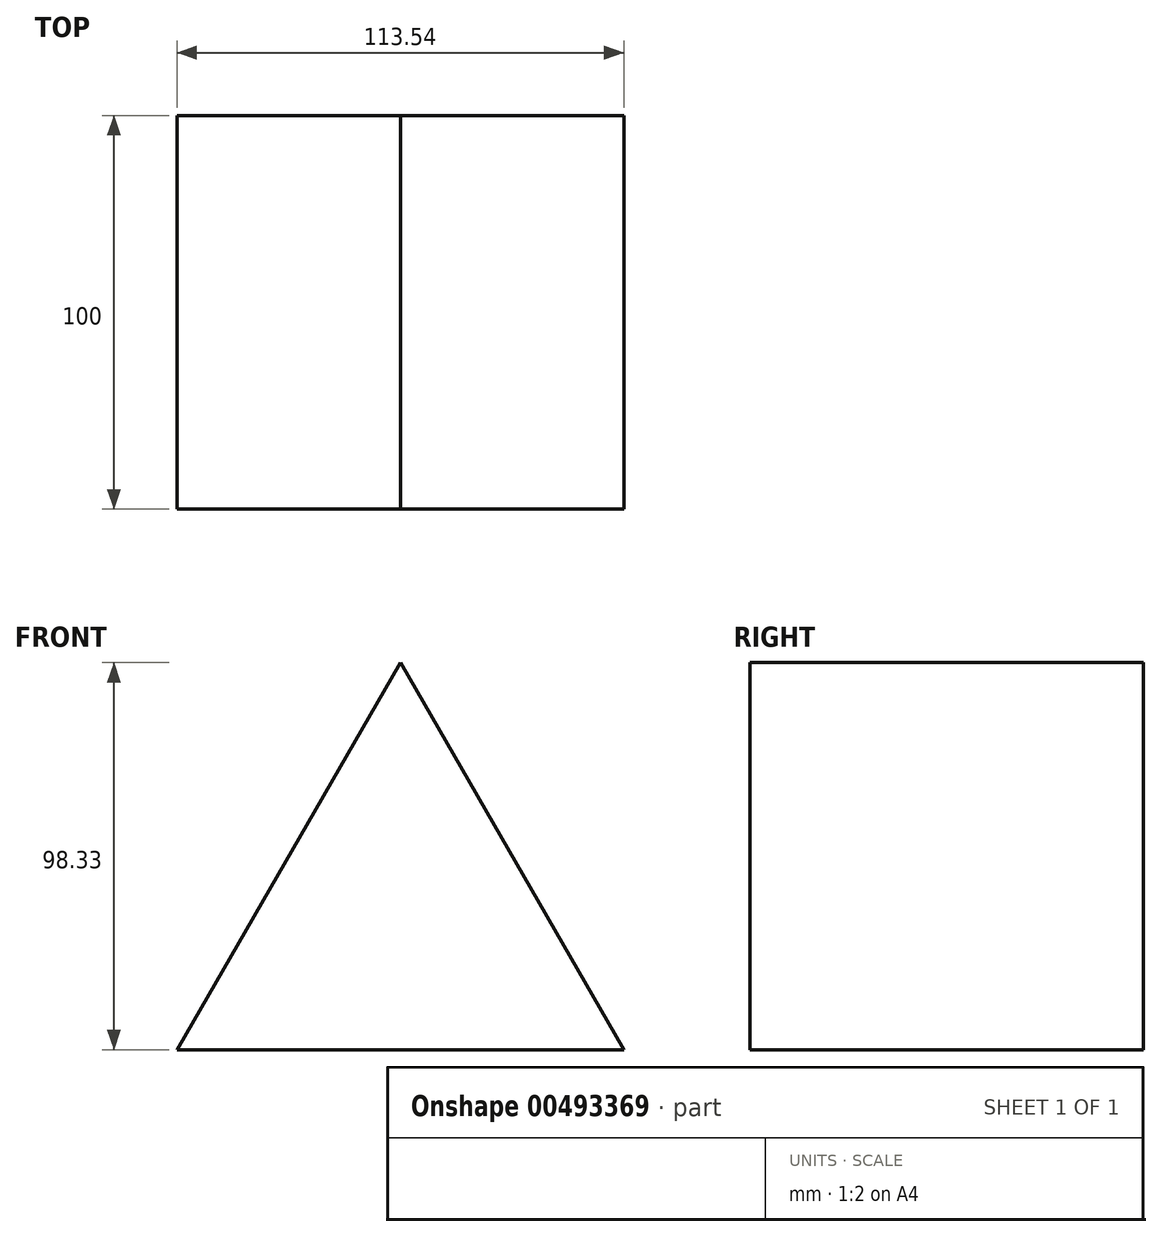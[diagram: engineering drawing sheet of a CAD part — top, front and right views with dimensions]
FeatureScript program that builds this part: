
annotation { "Feature Type Name" : "Feature", "Feature Type Description" : "" }
export const myFeature = defineFeature(function(context is Context, id is Id, definition is map)
    precondition{}
    {
        {
            var Q0;
            Q0=qCreatedBy(makeId("Front.planeOp"),FACE);
            var sketch = newSketch(context, id + "F0", { "sketchPlane" : qUnion([Q0])});
            skCircle(sketch, "E0.cCircle", {"center": v(0, 0) * mm, "radius": 65.55 * mm, "construction": true});
            skLineSegment(sketch, "E0.0", {"start": v(0, 65.55) * mm, "end": v(56.77, -32.78) * mm});
            skLineSegment(sketch, "E0.1", {"start": v(56.77, -32.78) * mm, "end": v(-56.77, -32.78) * mm});
            skLineSegment(sketch, "E0.2", {"start": v(-56.77, -32.78) * mm, "end": v(0, 65.55) * mm});
            skSolve(sketch);
        }
        {
            var Q0;
            Q0 = qSketchRegion(id + "F0", true);
            extrude(context, id + "F1", {"entities" : qUnion([Q0]), "endBound" : BoundingType.SYMMETRIC, "depth" : 100 * mm});
        }
    });
